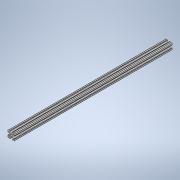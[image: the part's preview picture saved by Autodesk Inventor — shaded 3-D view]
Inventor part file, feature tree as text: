
AUTODESK INVENTOR PART (.ipt)
format: ipt  version: 2020 (Build 240168000, 168)  size: 238,080 bytes
history: native  units: in
note: dims shown in document units (in); Inventor stores cm internally (conversion verified against a paired STEP export)
features: extrude x1, sketch x1
ambient origin geometry x8: Origin, YZ Plane, XZ Plane, XY Plane, X Axis, Y Axis, Z Axis, Center Point
bodies: Solid1 (feature_tree)
feature tree (2):
  extrude  "Extrusion1"  [1 undecoded]
  sketch  "Sketch1"  dims[d0=23.0in d1=0.0in]
note: 1 required parameter value undecoded (feature->parameter linkage not recoverable at this tier; creation-order binding heuristic only, values carry confidence <= 0.55)
